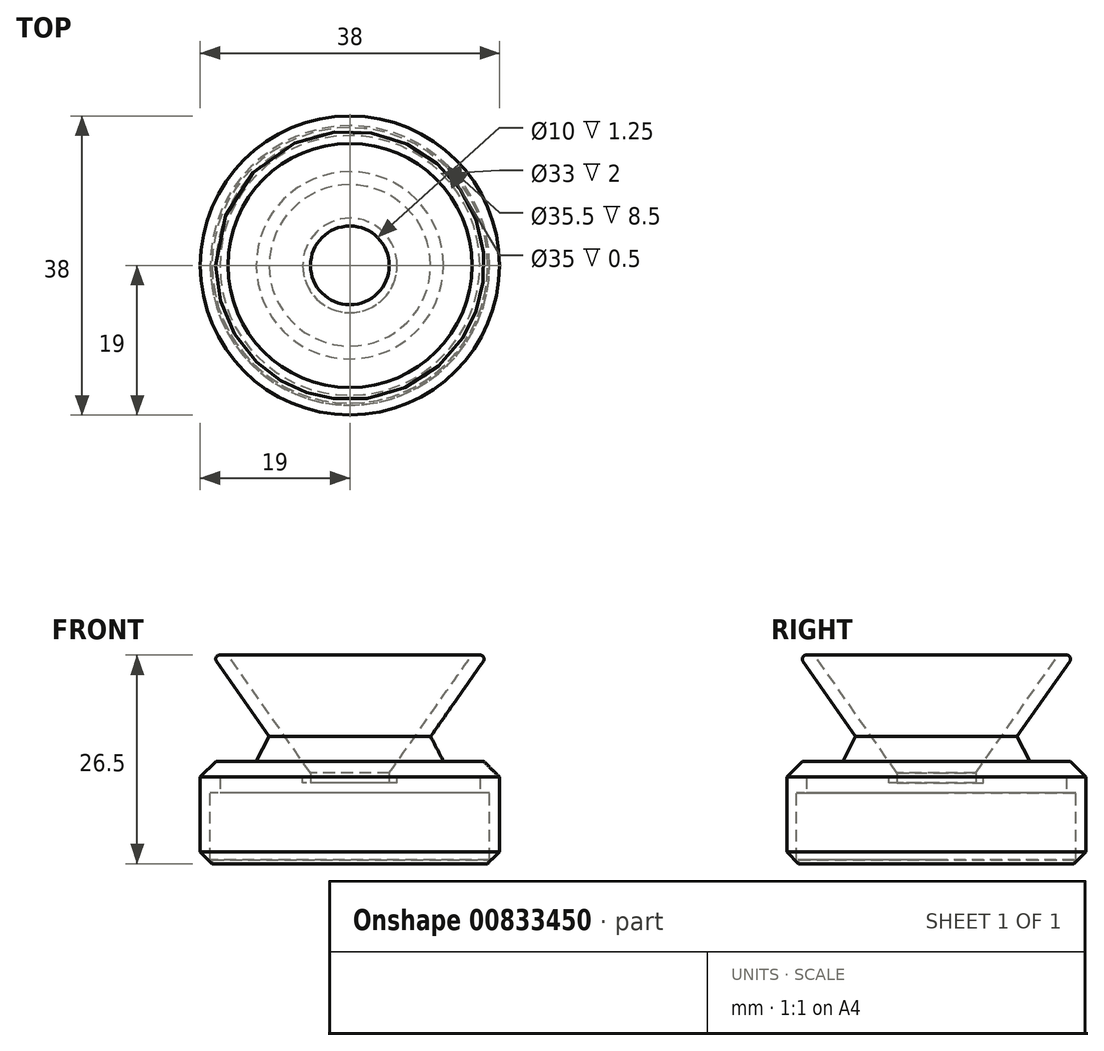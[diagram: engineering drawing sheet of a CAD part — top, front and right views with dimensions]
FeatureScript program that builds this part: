
annotation { "Feature Type Name" : "Feature", "Feature Type Description" : "" }
export const myFeature = defineFeature(function(context is Context, id is Id, definition is map)
    precondition{}
    {
        {
            var Q0;
            Q0=qCreatedBy(makeId("Top.planeOp"),FACE);
            var sketch = newSketch(context, id + "F0", { "sketchPlane" : qUnion([Q0])});
            skCircle(sketch, "E0", {"center": v(0, 0) * mm, "radius": 17.75 * mm});
            skCircle(sketch, "E1", {"center": v(0, 0) * mm, "radius": 5 * mm});
            skCircle(sketch, "E2", {"center": v(0, 0) * mm, "radius": 19 * mm});
            skCircle(sketch, "E3", {"center": v(0, 0) * mm, "radius": 16.5 * mm});
            skSolve(sketch);
        }
        {
            var Q0;
            Q0 = qSketchRegion(id + "F0", true);
            extrude(context, id + "F1", {"entities" : qUnion([Q0]), "oppositeDirection" : true, "depth" : 9.5 * mm, "offsetDistance" : 25 * mm, "hasSecondDirection" : true, "secondDirectionOppositeDirection" : false, "secondDirectionDepth" : 2 * mm});
        }
        {
            var Q0;
            Q0=makeQuery(id+"F1.opExtrude","CAP_FACE",FACE,{"disambiguationData":[OSD([sQuery(id+"F0.wireOp",EDGE,"E0"),sQuery(id+"F0.wireOp",EDGE,"E2")])],"isStart":false});
            var sketch = newSketch(context, id + "F2", { "sketchPlane" : qUnion([Q0])});
            skCircle(sketch, "E4", {"center": v(0, 0) * mm, "radius": 17.5 * mm});
            skSolve(sketch);
        }
        {
            var Q0;
            Q0=makeQuery(id+"F2.imprint","IMPRINT",FACE,{"disambiguationData":[TD([[makeQuery(id+"F2.imprint","IMPRINT",EDGE,{"derivedFrom":sQuery(id+"F2.wireOp",EDGE,"E4")}),-1.0]])]});
            extrude(context, id + "F3", {"entities" : qUnion([Q0]), "operationType" : NewBodyOperationType.ADD, "oppositeDirection" : true, "depth" : 1 * mm, "offsetDistance" : 25 * mm});
        }
        {
            var Q0;
            Q0=makeQuery(id+"F0.imprint","IMPRINT",FACE,{"disambiguationData":[TD([[makeQuery(id+"F0.imprint","IMPRINT",EDGE,{"derivedFrom":sQuery(id+"F0.wireOp",EDGE,"E0")}),1.0]])]});
            extrude(context, id + "F4", {"entities" : qUnion([Q0]), "operationType" : NewBodyOperationType.ADD, "depth" : 2.5 * mm, "offsetDistance" : 25 * mm});
        }
        {
            var Q0;
            {var subQ0=sQuery(id+"F0.wireOp",EDGE,"E0");Q0=makeQuery(id+"F4.boolean.opBoolean","MERGE",FACE,{"derivedFrom":[makeQuery(id+"F1.opExtrude","CAP_FACE",FACE,{"disambiguationData":[OSD([subQ0,sQuery(id+"F0.wireOp",EDGE,"E2")])],"isStart":true}),makeQuery(id+"F4.opExtrude","CAP_FACE",FACE,{"disambiguationData":[OSD([subQ0,sQuery(id+"F0.wireOp",EDGE,"E3")])],"isStart":false})]});}
            var sketch = newSketch(context, id + "F5", { "sketchPlane" : qUnion([Q0])});
            skCircle(sketch, "E5", {"center": v(0, 0) * mm, "radius": 19 * mm});
            skSolve(sketch);
        }
        {
            var Q0;
            Q0 = qSketchRegion(id + "F5", true);
            extrude(context, id + "F6", {"entities" : qUnion([Q0]), "operationType" : NewBodyOperationType.ADD, "depth" : 2 * mm, "offsetDistance" : 25 * mm});
        }
        {
            var Q0;
            Q0=makeQuery(id+"F0.imprint","IMPRINT",FACE,{"disambiguationData":[TD([[makeQuery(id+"F0.imprint","IMPRINT",EDGE,{"derivedFrom":sQuery(id+"F0.wireOp",EDGE,"E1")}),1.0]])]});
            extrude(context, id + "F7", {"entities" : qUnion([Q0]), "operationType" : NewBodyOperationType.REMOVE, "depth" : 25 * mm, "offsetDistance" : 25 * mm});
        }
        {
            var Q0;
            Q0=makeQuery(id+"F6.opExtrude","CAP_FACE",FACE,{"disambiguationData":[OSD([sQuery(id+"F5.wireOp",EDGE,"E5")])],"isStart":true});
            var sketch = newSketch(context, id + "F8", { "sketchPlane" : qUnion([Q0])});
            skCircle(sketch, "E6", {"center": v(0, 0) * mm, "radius": 6 * mm});
            skCircle(sketch, "E7", {"center": v(0, 0) * mm, "radius": 5 * mm});
            skSolve(sketch);
        }
        {
            var Q0;
            Q0 = qSketchRegion(id + "F8", true);
            extrude(context, id + "F9", {"entities" : qUnion([Q0]), "operationType" : NewBodyOperationType.ADD, "depth" : .75 * mm, "offsetDistance" : 25 * mm});
        }
        {
            var Q0;
            Q0=qCreatedBy(makeId("Right.planeOp"),FACE);
            var sketch = newSketch(context, id + "F10", { "sketchPlane" : qUnion([Q0])});
            skLineSegment(sketch, "E8", {"start": v(5, 2.5) * mm, "end": v(0, 2.5) * mm});
            skLineSegment(sketch, "E9", {"start": v(0, 2.5) * mm, "end": v(0, 17.5) * mm});
            skLineSegment(sketch, "E10", {"start": v(0, 17.5) * mm, "end": v(16.54, 17.5) * mm});
            skLineSegment(sketch, "E11", {"start": v(5, 2.5) * mm, "end": v(7, 2.5) * mm});
            skLineSegment(sketch, "E12", {"start": v(7, 2.5) * mm, "end": v(16.95, 16.71) * mm});
            skLineSegment(sketch, "E13", {"start": v(5, 2.5) * mm, "end": v(15.5, 17.5) * mm});
            skPoint(sketch, "E14.visualSharp", {"position": v(17.5, 17.5) * mm});
            skArc(sketch, "E14.filletArc", {"start": v(16.95, 16.71) * mm, "mid": v(16.98, 17.23) * mm, "end": v(16.54, 17.5) * mm});
            skSolve(sketch);
        }
        {
            var Q0;
            Q0=makeQuery(id+"F10.imprint","IMPRINT",FACE,{"disambiguationData":[TD([[makeQuery(id+"F10.imprint","IMPRINT",EDGE,{"derivedFrom":sQuery(id+"F10.wireOp",EDGE,"E11")}),1.0]])]});
            var Q1;
            Q1=sQuery(id+"F10.wireOp",EDGE,"E9");
            revolve(context, id + "F11", {"operationType" : NewBodyOperationType.ADD, "surfaceOperationType" : NewSurfaceOperationType.NEW, "entities" : qUnion([Q0]), "axis" : qUnion([Q1]), "revolveType" : RevolveType.FULL});
        }
        {
            var Q0;
            Q0=makeQuery(id+"F10.imprint","IMPRINT",FACE,{"disambiguationData":[TD([[makeQuery(id+"F10.imprint","IMPRINT",EDGE,{"derivedFrom":sQuery(id+"F10.wireOp",EDGE,"E8")}),-1.0]])]});
            var Q1;
            Q1=sQuery(id+"F10.wireOp",EDGE,"E9");
            revolve(context, id + "F12", {"operationType" : NewBodyOperationType.REMOVE, "surfaceOperationType" : NewSurfaceOperationType.NEW, "entities" : qUnion([Q0]), "axis" : qUnion([Q1]), "revolveType" : RevolveType.FULL, "oppositeDirection" : true});
        }
        {
            var Q0;
            Q0=makeQuery(id+"F11.boolean.opBoolean","INTERSECT",EDGE,{"derivedFrom":[makeQuery(id+"F6.opExtrude","CAP_FACE",FACE,{"disambiguationData":[OSD([sQuery(id+"F5.wireOp",EDGE,"E5")])],"isStart":false}),makeQuery(id+"F11.opRevolve","SWEPT_FACE",FACE,{"disambiguationData":[OSD([sQuery(id+"F10.wireOp",EDGE,"E12")])]})]});
            var Q1;
            Q1=makeQuery(id+"F6.opExtrude","CAP_EDGE",EDGE,{"disambiguationData":[OSD([sQuery(id+"F5.wireOp",EDGE,"E5")])],"isStart":false});
            var Q2;
            Q2=makeQuery(id+"F1.opExtrude","CAP_EDGE",EDGE,{"disambiguationData":[OSD([sQuery(id+"F0.wireOp",EDGE,"E2")])],"isStart":false});
            chamfer(context, id + "F13", {"entities" : qUnion([Q0, Q1, Q2]), "width" : 2 * mm, "tangentPropagation" : true});
        }
    });
